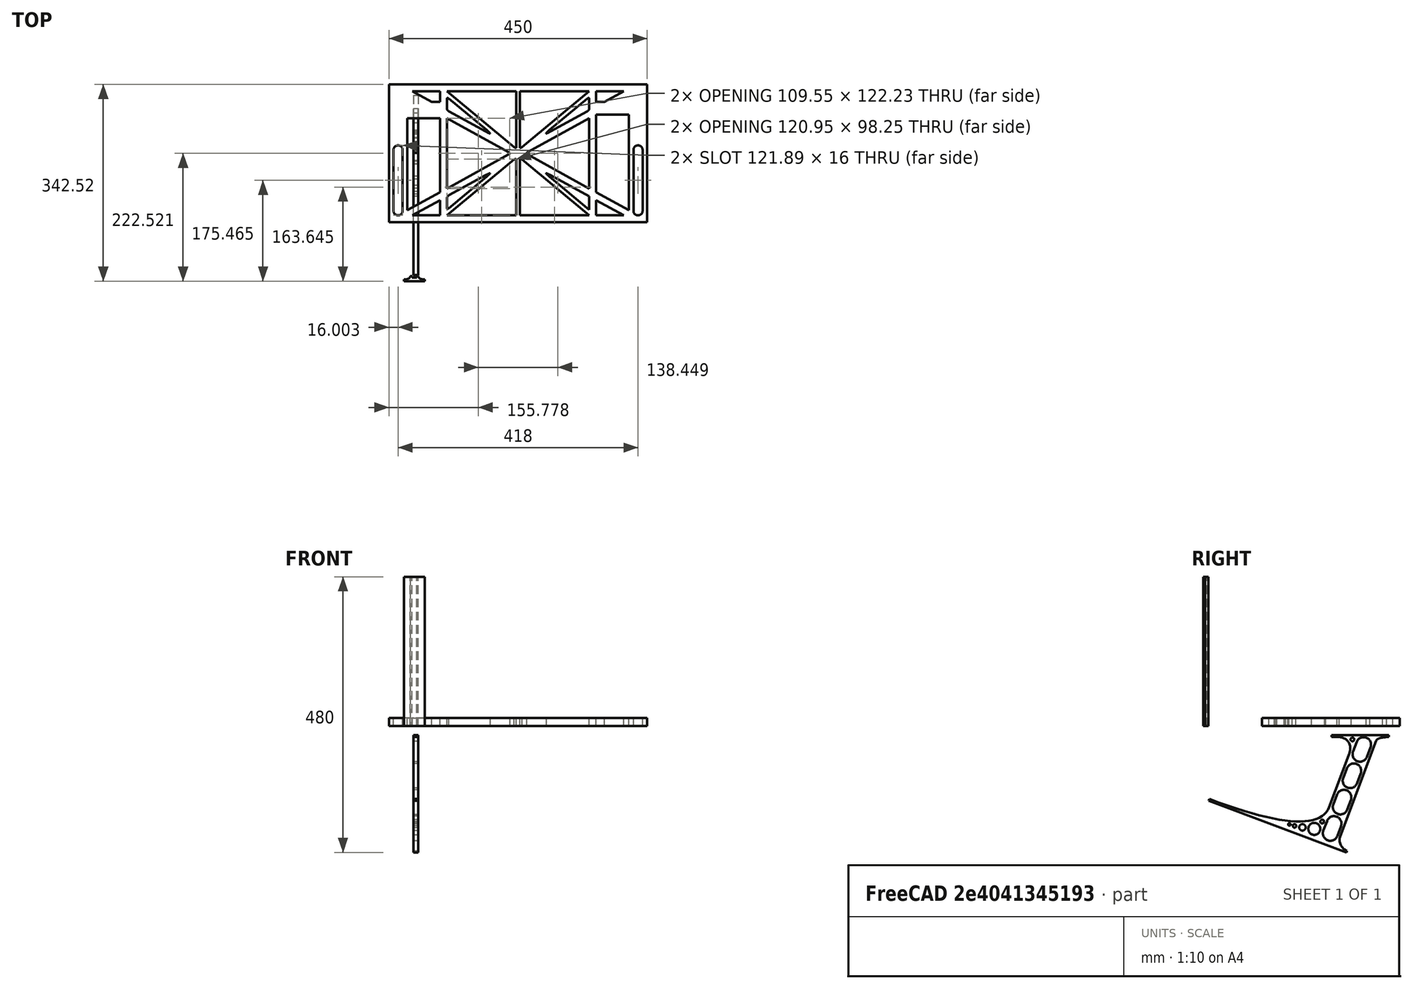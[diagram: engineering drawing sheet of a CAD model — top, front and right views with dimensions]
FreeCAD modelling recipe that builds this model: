
FCSTD DOCUMENT  (FreeCAD 0.19R0.19.2)
Label: laptopStand074
License: All rights reserved
LicenseURL: http://en.wikipedia.org/wiki/All_rights_reserved
objects: Sketcher::SketchObject×3, Part::Extrusion×3
note: 6 computed .brp shape members not serialized (recipe doc carries the construction recipe); baked Part::Feature solids carry a one-line shape summary decoded from their .brp

FEATURE [Sketcher::SketchObject] Sketch
  FullyConstrained = true
  sketch-geometry (164):
    g0: LineSegment StartX=-10.9272 StartY=-82.7794 StartZ=0 EndX=46.0728 EndY=-51.4823 EndZ=0
    g1: LineSegment StartX=366.073 StartY=-91.7794 StartZ=0 EndX=318.073 EndY=-65.424 EndZ=0
    g2: LineSegment StartX=-10.9272 StartY=77.3346 StartZ=0 EndX=-10.9272 EndY=-82.7794 EndZ=0
    g3: LineSegment StartX=375.073 StartY=-82.7794 StartZ=0 EndX=375.073 EndY=83.9235 EndZ=0
    g4: LineSegment StartX=-1.92719 StartY=-91.7794 StartZ=0 EndX=46.0728 EndY=-91.7794 EndZ=0
    g5: LineSegment StartX=318.073 StartY=124.221 StartZ=0 EndX=366.073 EndY=124.221 EndZ=0
    g6: LineSegment StartX=306.073 StartY=124.221 StartZ=0 EndX=189.124 EndY=27.0628 EndZ=0
    g7: LineSegment StartX=58.0728 StartY=-91.7794 StartZ=0 EndX=175.022 EndY=5.37834 EndZ=0
    g8: LineSegment StartX=58.0728 StartY=-81.8102 StartZ=0 EndX=58.0728 EndY=-58.8351 EndZ=0
    g9: LineSegment StartX=175.022 StartY=27.0628 StartZ=0 EndX=58.0728 EndY=124.221 EndZ=0
    g10: LineSegment StartX=189.124 StartY=5.37834 StartZ=0 EndX=306.073 EndY=-91.7794 EndZ=0
    g11: LineSegment StartX=306.073 StartY=77.3346 StartZ=0 EndX=306.073 EndY=-44.8935 EndZ=0
    g12: LineSegment StartX=318.073 StartY=83.9235 StartZ=0 EndX=318.073 EndY=-51.4823 EndZ=0
    g13: LineSegment StartX=306.073 StartY=-58.8351 StartZ=0 EndX=306.073 EndY=-81.8102 EndZ=0
    g14: LineSegment StartX=318.073 StartY=-51.4823 StartZ=0 EndX=375.073 EndY=-82.7794 EndZ=0
    g15: LineSegment StartX=318.073 StartY=-65.424 StartZ=0 EndX=318.073 EndY=-91.7794 EndZ=0
    g16: LineSegment StartX=318.073 StartY=-91.7794 StartZ=0 EndX=366.073 EndY=-91.7794 EndZ=0
    g17: LineSegment StartX=58.0728 StartY=-44.8935 StartZ=0 EndX=58.0728 EndY=77.3346 EndZ=0
    g18: LineSegment StartX=46.0728 StartY=-65.424 StartZ=0 EndX=-1.92719 EndY=-91.7794 EndZ=0
    g19: LineSegment StartX=46.0728 StartY=-65.424 StartZ=0 EndX=46.0728 EndY=-91.7794 EndZ=0
    g20: LineSegment StartX=46.0728 StartY=77.3346 StartZ=0 EndX=46.0728 EndY=-51.4823 EndZ=0
    g21: LineSegment StartX=-42.9272 StartY=136.221 StartZ=0 EndX=-42.9272 EndY=-103.779 EndZ=0
    g22: LineSegment StartX=407.073 StartY=136.221 StartZ=0 EndX=407.073 EndY=-103.779 EndZ=0
    g23: LineSegment StartX=179.022 StartY=27.0628 StartZ=0 EndX=179.022 EndY=124.221 EndZ=0
    g24: LineSegment StartX=185.124 StartY=27.0628 StartZ=0 EndX=185.124 EndY=124.221 EndZ=0
    g25: ArcOfCircle CenterX=-26.9272 CenterY=22.1087 CenterZ=0 NormalX=0 NormalY=0 NormalZ=1 AngleXU=0 Radius=8 StartAngle=1e-16 EndAngle=3.14159
    g26: ArcOfCircle CenterX=-26.9272 CenterY=-83.7794 CenterZ=0 NormalX=0 NormalY=0 NormalZ=1 AngleXU=0 Radius=8 StartAngle=3.14159 EndAngle=6.28319
    g27: LineSegment StartX=-34.9272 StartY=22.1087 StartZ=0 EndX=-34.9272 EndY=-83.7794 EndZ=0
    g28: LineSegment StartX=-18.9272 StartY=22.1087 StartZ=0 EndX=-18.9272 EndY=-83.7794 EndZ=0
    g29: LineSegment StartX=185.124 StartY=-91.7794 StartZ=0 EndX=306.073 EndY=-91.7794 EndZ=0
    g30: LineSegment StartX=179.022 StartY=-91.7794 StartZ=0 EndX=58.0728 EndY=-91.7794 EndZ=0
    g31: LineSegment StartX=306.073 StartY=124.221 StartZ=0 EndX=185.124 EndY=124.221 EndZ=0
    g32: LineSegment StartX=179.022 StartY=124.221 StartZ=0 EndX=58.0728 EndY=124.221 EndZ=0
    g33: ArcOfCircle CenterX=391.073 CenterY=22.1087 CenterZ=0 NormalX=0 NormalY=0 NormalZ=1 AngleXU=0 Radius=8 StartAngle=-4.4e-15 EndAngle=3.14159
    g34: LineSegment StartX=399.073 StartY=22.1087 StartZ=0 EndX=399.073 EndY=-83.7794 EndZ=0
    g35: LineSegment StartX=383.073 StartY=22.1087 StartZ=0 EndX=383.073 EndY=-83.7794 EndZ=0
    g36: ArcOfCircle CenterX=391.073 CenterY=-83.7794 CenterZ=0 NormalX=0 NormalY=0 NormalZ=1 AngleXU=0 Radius=8 StartAngle=3.14159 EndAngle=6.28319
    g37: Circle CenterX=175.022 CenterY=27.0628 CenterZ=0 NormalX=0 NormalY=0 NormalZ=1 AngleXU=0 Radius=1
    g38: Circle CenterX=179.022 CenterY=24.8665 CenterZ=0 NormalX=0 NormalY=0 NormalZ=1 AngleXU=0 Radius=1
    g39: Circle CenterX=179.022 CenterY=27.0628 CenterZ=0 NormalX=0 NormalY=0 NormalZ=1 AngleXU=0 Radius=1
    g40: BSplineCurve PolesCount=3 KnotsCount=2 Degree=2 IsPeriodic=0
    g41: GeomPoint X=175.022 Y=27.0628 Z=0
    g42: GeomPoint X=179.022 Y=27.0628 Z=0
    g43: Circle CenterX=189.124 CenterY=27.0628 CenterZ=0 NormalX=0 NormalY=0 NormalZ=1 AngleXU=0 Radius=1
    g44: Circle CenterX=185.124 CenterY=24.8665 CenterZ=0 NormalX=0 NormalY=0 NormalZ=1 AngleXU=0 Radius=1
    g45: Circle CenterX=185.124 CenterY=27.0628 CenterZ=0 NormalX=0 NormalY=0 NormalZ=1 AngleXU=0 Radius=1
    g46: BSplineCurve PolesCount=3 KnotsCount=2 Degree=2 IsPeriodic=0
    g47: GeomPoint X=189.124 Y=27.0628 Z=0
    g48: GeomPoint X=185.124 Y=27.0628 Z=0
    g49: Circle CenterX=175.022 CenterY=5.37834 CenterZ=0 NormalX=0 NormalY=0 NormalZ=1 AngleXU=0 Radius=1
    g50: Circle CenterX=179.022 CenterY=7.57463 CenterZ=0 NormalX=0 NormalY=0 NormalZ=1 AngleXU=0 Radius=1
    g51: Circle CenterX=179.022 CenterY=5.34704 CenterZ=0 NormalX=0 NormalY=0 NormalZ=1 AngleXU=0 Radius=1
    g52: BSplineCurve PolesCount=3 KnotsCount=2 Degree=2 IsPeriodic=0
    g53: GeomPoint X=175.022 Y=5.37834 Z=0
    g54: GeomPoint X=179.022 Y=5.34704 Z=0
    g55: Circle CenterX=189.124 CenterY=5.37834 CenterZ=0 NormalX=0 NormalY=0 NormalZ=1 AngleXU=0 Radius=1
    g56: Circle CenterX=185.124 CenterY=7.57463 CenterZ=0 NormalX=0 NormalY=0 NormalZ=1 AngleXU=0 Radius=1
    g57: Circle CenterX=185.124 CenterY=5.34704 CenterZ=0 NormalX=0 NormalY=0 NormalZ=1 AngleXU=0 Radius=1
    g58: BSplineCurve PolesCount=3 KnotsCount=2 Degree=2 IsPeriodic=0
    g59: GeomPoint X=189.124 Y=5.37834 Z=0
    g60: GeomPoint X=185.124 Y=5.34704 Z=0
    g61: LineSegment StartX=179.022 StartY=5.34704 StartZ=0 EndX=179.022 EndY=-91.7794 EndZ=0
    g62: LineSegment StartX=185.124 StartY=-91.7794 StartZ=0 EndX=185.124 EndY=5.34704 EndZ=0
    g63: Circle CenterX=165.871 CenterY=18.1458 CenterZ=0 NormalX=0 NormalY=0 NormalZ=1 AngleXU=0 Radius=1
    g64: Circle CenterX=169.377 CenterY=16.2206 CenterZ=0 NormalX=0 NormalY=0 NormalZ=1 AngleXU=0 Radius=1
    g65: Circle CenterX=165.871 CenterY=14.2954 CenterZ=0 NormalX=0 NormalY=0 NormalZ=1 AngleXU=0 Radius=1
    g66: BSplineCurve PolesCount=3 KnotsCount=2 Degree=2 IsPeriodic=0
    g67: GeomPoint X=165.871 Y=18.1458 Z=0
    g68: GeomPoint X=165.871 Y=14.2954 Z=0
    g69: Circle CenterX=198.275 CenterY=18.1458 CenterZ=0 NormalX=0 NormalY=0 NormalZ=1 AngleXU=0 Radius=1
    g70: Circle CenterX=194.768 CenterY=16.2206 CenterZ=0 NormalX=0 NormalY=0 NormalZ=1 AngleXU=0 Radius=1
    g71: Circle CenterX=198.275 CenterY=14.2954 CenterZ=0 NormalX=0 NormalY=0 NormalZ=1 AngleXU=0 Radius=1
    g72: BSplineCurve PolesCount=3 KnotsCount=2 Degree=2 IsPeriodic=0
    g73: GeomPoint X=198.275 Y=18.1458 Z=0
    g74: GeomPoint X=198.275 Y=14.2954 Z=0
    g75: LineSegment StartX=165.871 StartY=18.1458 StartZ=0 EndX=58.0728 EndY=77.3346 EndZ=0
    g76: LineSegment StartX=58.0728 StartY=-44.8935 StartZ=0 EndX=165.871 EndY=14.2954 EndZ=0
    g77: LineSegment StartX=198.275 StartY=18.1458 StartZ=0 EndX=306.073 EndY=77.3346 EndZ=0
    g78: LineSegment StartX=198.275 StartY=14.2954 StartZ=0 EndX=306.073 EndY=-44.8935 EndZ=0
    g79: LineSegment StartX=407.073 StartY=-103.779 StartZ=0 EndX=-42.9272 EndY=-103.779 EndZ=0
    g80: LineSegment StartX=407.073 StartY=136.221 StartZ=0 EndX=-42.9272 EndY=136.221 EndZ=0
    g81: LineSegment StartX=46.0728 StartY=77.3346 StartZ=0 EndX=-10.9272 EndY=77.3346 EndZ=0
    g82: LineSegment StartX=46.0728 StartY=105.865 StartZ=0 EndX=31.5028 EndY=105.865 EndZ=0
    g83: LineSegment StartX=46.0728 StartY=124.221 StartZ=0 EndX=46.0728 EndY=105.865 EndZ=0
    g84: LineSegment StartX=-1.92719 StartY=124.221 StartZ=0 EndX=31.5028 EndY=105.865 EndZ=0
    g85: LineSegment StartX=46.0728 StartY=124.221 StartZ=0 EndX=-1.92719 EndY=124.221 EndZ=0
    g86: LineSegment StartX=318.073 StartY=83.9235 StartZ=0 EndX=375.073 EndY=83.9235 EndZ=0
    g87: LineSegment StartX=318.073 StartY=105.865 StartZ=0 EndX=332.643 EndY=105.865 EndZ=0
    g88: LineSegment StartX=332.643 StartY=105.865 StartZ=0 EndX=366.073 EndY=124.221 EndZ=0
    g89: LineSegment StartX=318.073 StartY=124.221 StartZ=0 EndX=318.073 EndY=105.865 EndZ=0
    g90: Circle CenterX=125.607 CenterY=54.1951 CenterZ=0 NormalX=0 NormalY=0 NormalZ=1 AngleXU=0 Radius=1
    g91: Circle CenterX=139.632 CenterY=46.4944 CenterZ=0 NormalX=0 NormalY=0 NormalZ=1 AngleXU=0 Radius=1
    g92: Circle CenterX=127.326 CenterY=56.7187 CenterZ=0 NormalX=0 NormalY=0 NormalZ=1 AngleXU=0 Radius=1
    g93: BSplineCurve PolesCount=3 KnotsCount=2 Degree=2 IsPeriodic=0
    g94: GeomPoint X=125.607 Y=54.1951 Z=0
    g95: GeomPoint X=127.326 Y=56.7187 Z=0
    g96: Circle CenterX=236.821 CenterY=56.7187 CenterZ=0 NormalX=0 NormalY=0 NormalZ=1 AngleXU=0 Radius=1
    g97: Circle CenterX=224.513 CenterY=46.4944 CenterZ=0 NormalX=0 NormalY=0 NormalZ=1 AngleXU=0 Radius=1
    g98: Circle CenterX=238.538 CenterY=54.1951 CenterZ=0 NormalX=0 NormalY=0 NormalZ=1 AngleXU=0 Radius=1
    g99: BSplineCurve PolesCount=3 KnotsCount=2 Degree=2 IsPeriodic=0
    g100: GeomPoint X=236.821 Y=56.7187 Z=0
    g101: GeomPoint X=238.538 Y=54.1951 Z=0
    g102: Circle CenterX=238.538 CenterY=-21.7539 CenterZ=0 NormalX=0 NormalY=0 NormalZ=1 AngleXU=0 Radius=1
    g103: Circle CenterX=224.513 CenterY=-14.0532 CenterZ=0 NormalX=0 NormalY=0 NormalZ=1 AngleXU=0 Radius=1
    g104: Circle CenterX=236.821 CenterY=-24.2775 CenterZ=0 NormalX=0 NormalY=0 NormalZ=1 AngleXU=0 Radius=1
    g105: BSplineCurve PolesCount=3 KnotsCount=2 Degree=2 IsPeriodic=0
    g106: GeomPoint X=238.538 Y=-21.7539 Z=0
    g107: GeomPoint X=236.821 Y=-24.2775 Z=0
    g108: LineSegment StartX=238.538 StartY=-21.7539 StartZ=0 EndX=306.073 EndY=-58.8351 EndZ=0
    g109: LineSegment StartX=236.821 StartY=-24.2775 StartZ=0 EndX=306.073 EndY=-81.8102 EndZ=0
    g110: Circle CenterX=125.607 CenterY=-21.7539 CenterZ=0 NormalX=0 NormalY=0 NormalZ=1 AngleXU=0 Radius=1
    g111: Circle CenterX=139.632 CenterY=-14.0532 CenterZ=0 NormalX=0 NormalY=0 NormalZ=1 AngleXU=0 Radius=1
    g112: Circle CenterX=127.325 CenterY=-24.2775 CenterZ=0 NormalX=0 NormalY=0 NormalZ=1 AngleXU=0 Radius=1
    g113: BSplineCurve PolesCount=3 KnotsCount=2 Degree=2 IsPeriodic=0
    g114: GeomPoint X=125.607 Y=-21.7539 Z=0
    g115: GeomPoint X=127.325 Y=-24.2775 Z=0
    g116: LineSegment StartX=125.607 StartY=-21.7539 StartZ=0 EndX=58.0728 EndY=-58.8351 EndZ=0
    g117: LineSegment StartX=127.325 StartY=-24.2775 StartZ=0 EndX=58.0728 EndY=-81.8102 EndZ=0
    g118: Circle CenterX=302.996 CenterY=111.695 CenterZ=0 NormalX=0 NormalY=0 NormalZ=1 AngleXU=0 Radius=1
    g119: Circle CenterX=306.073 CenterY=114.251 CenterZ=0 NormalX=0 NormalY=0 NormalZ=1 AngleXU=0 Radius=1
    g120: Circle CenterX=306.073 CenterY=110.251 CenterZ=0 NormalX=0 NormalY=0 NormalZ=1 AngleXU=0 Radius=1
    g121: BSplineCurve PolesCount=3 KnotsCount=2 Degree=2 IsPeriodic=0
    g122: GeomPoint X=302.996 Y=111.695 Z=0
    g123: GeomPoint X=306.073 Y=110.251 Z=0
    g124: Circle CenterX=306.073 CenterY=95.2763 CenterZ=0 NormalX=0 NormalY=0 NormalZ=1 AngleXU=0 Radius=1
    g125: Circle CenterX=306.073 CenterY=91.2763 CenterZ=0 NormalX=0 NormalY=0 NormalZ=1 AngleXU=0 Radius=1
    g126: Circle CenterX=302.567 CenterY=89.3511 CenterZ=0 NormalX=0 NormalY=0 NormalZ=1 AngleXU=0 Radius=1
    g127: BSplineCurve PolesCount=3 KnotsCount=2 Degree=2 IsPeriodic=0
    g128: GeomPoint X=306.073 Y=95.2763 Z=0
    g129: GeomPoint X=302.567 Y=89.3511 Z=0
    g130: LineSegment StartX=306.073 StartY=110.251 StartZ=0 EndX=306.073 EndY=95.2763 EndZ=0
    g131: LineSegment StartX=302.996 StartY=111.695 StartZ=0 EndX=236.821 EndY=56.7187 EndZ=0
    g132: LineSegment StartX=238.538 StartY=54.1951 StartZ=0 EndX=302.567 EndY=89.3511 EndZ=0
    g133: Circle CenterX=61.1496 CenterY=111.695 CenterZ=0 NormalX=0 NormalY=0 NormalZ=1 AngleXU=0 Radius=1
    g134: Circle CenterX=58.0728 CenterY=114.251 CenterZ=0 NormalX=0 NormalY=0 NormalZ=1 AngleXU=0 Radius=1
    g135: Circle CenterX=58.0728 CenterY=110.251 CenterZ=0 NormalX=0 NormalY=0 NormalZ=1 AngleXU=0 Radius=1
    g136: BSplineCurve PolesCount=3 KnotsCount=2 Degree=2 IsPeriodic=0
    g137: GeomPoint X=61.1496 Y=111.695 Z=0
    g138: GeomPoint X=58.0728 Y=110.251 Z=0
    g139: Circle CenterX=61.5791 CenterY=89.3511 CenterZ=0 NormalX=0 NormalY=0 NormalZ=1 AngleXU=0 Radius=1
    g140: Circle CenterX=58.0728 CenterY=91.2763 CenterZ=0 NormalX=0 NormalY=0 NormalZ=1 AngleXU=0 Radius=1
    g141: Circle CenterX=58.0728 CenterY=95.2763 CenterZ=0 NormalX=0 NormalY=0 NormalZ=1 AngleXU=0 Radius=1
    g142: BSplineCurve PolesCount=3 KnotsCount=2 Degree=2 IsPeriodic=0
    g143: GeomPoint X=61.5791 Y=89.3511 Z=0
    g144: GeomPoint X=58.0728 Y=95.2763 Z=0
    g145: LineSegment StartX=58.0728 StartY=110.251 StartZ=0 EndX=58.0728 EndY=95.2763 EndZ=0
    g146: LineSegment StartX=61.1496 StartY=111.695 StartZ=0 EndX=127.326 EndY=56.7187 EndZ=0
    g147: LineSegment StartX=125.607 StartY=54.1951 StartZ=0 EndX=61.5791 EndY=89.3511 EndZ=0
    g148: LineSegment StartX=58.0728 StartY=-58.8351 StartZ=0 EndX=58.0728 EndY=-62.8351 EndZ=0
    g149: LineSegment StartX=58.0728 StartY=-58.8351 StartZ=0 EndX=61.5791 EndY=-56.9099 EndZ=0
    g150: LineSegment StartX=58.0728 StartY=-81.8102 StartZ=0 EndX=61.1496 EndY=-79.2541 EndZ=0
    g151: LineSegment StartX=58.0728 StartY=-81.8102 StartZ=0 EndX=58.0728 EndY=-77.8102 EndZ=0
    g152: Circle CenterX=61.5791 CenterY=-56.9099 CenterZ=0 NormalX=0 NormalY=0 NormalZ=1 AngleXU=0 Radius=1
    g153: Circle CenterX=58.0728 CenterY=-58.8351 CenterZ=0 NormalX=0 NormalY=0 NormalZ=1 AngleXU=0 Radius=1
    g154: Circle CenterX=58.0728 CenterY=-62.8351 CenterZ=0 NormalX=0 NormalY=0 NormalZ=1 AngleXU=0 Radius=1
    g155: BSplineCurve PolesCount=3 KnotsCount=2 Degree=2 IsPeriodic=0
    g156: GeomPoint X=61.5791 Y=-56.9099 Z=0
    g157: GeomPoint X=58.0728 Y=-62.8351 Z=0
    g158: Circle CenterX=58.0728 CenterY=-77.8102 CenterZ=0 NormalX=0 NormalY=0 NormalZ=1 AngleXU=0 Radius=1
    g159: Circle CenterX=58.0728 CenterY=-81.8102 CenterZ=0 NormalX=0 NormalY=0 NormalZ=1 AngleXU=0 Radius=1
    g160: Circle CenterX=61.1496 CenterY=-79.2541 CenterZ=0 NormalX=0 NormalY=0 NormalZ=1 AngleXU=0 Radius=1
    g161: BSplineCurve PolesCount=3 KnotsCount=2 Degree=2 IsPeriodic=0
    g162: GeomPoint X=58.0728 Y=-77.8102 Z=0
    g163: GeomPoint X=61.1496 Y=-79.2541 Z=0
  constraints (295):
    c: Horizontal(g4)
    c: Horizontal(g5)
    c: Tangent(g11,g13)
    c: Coincident(g12,g14)
    c: Coincident(g15,g1)
    c: Tangent(g12,g15)
    c: Coincident(g19,g18)
    c: Coincident(g0,g20)
    c: Block(g9)
    c: Block(g6)
    c: Block(g14)
    c: Block(g3)
    c: Block(g13)
    c: Block(g1)
    c: Block(g15)
    c: Block(g10)
    c: Block(g7)
    c: Block(g19)
    c: Block(g18)
    c: Block(g0)
    c: Block(g2)
    c: Block(g11)
    c: Block(g5)
    c: Block(g16)
    c: Block(g4)
    c: Vertical(g21)
    c: Vertical(g22)
    c: Block(g22)
    c: Block(g21)
    c: Vertical(g23)
    c: Vertical(g24)
    c: Block(g23)
    c: Block(g24)
    c: Tangent(g25,g28) = 1.5708
    c: Tangent(g25,g27) = -1.5708
    c: Tangent(g27,g26) = -1.5708
    c: Tangent(g28,g26) = 1.5708
    c: Vertical(g27)
    c: Equal(g25,g26)
    c: Block(g28)
    c: Block(g27)
    c: Coincident(g29,g10)
    c: Horizontal(g29)
    c: Coincident(g30,g7)
    c: Horizontal(g30)
    c: Coincident(g31,g6)
    c: Coincident(g31,g24)
    c: Horizontal(g31)
    c: Coincident(g32,g23)
    c: Coincident(g32,g9)
    c: Horizontal(g32)
    c: Tangent(g33,g34) = 1.5708
    c: Tangent(g34,g36) = 1.5708
    c: Equal(g33,g36)
    c: Coincident(g35,g33)
    c: Coincident(g35,g36)
    c: Block(g34)
    c: Block(g35)
    c: Coincident(g40,g9)
    c: Weight(g37) = 1
    c: Equal(g37,g38)
    c: Equal(g37,g39)
    c: Coincident(g40,g23)
    c: InternalAlignment(g37,g40)
    c: InternalAlignment(g38,g40)
    c: InternalAlignment(g39,g40)
    c: InternalAlignment(g41,g40)
    c: InternalAlignment(g42,g40)
    c: Coincident(g46,g6)
    c: Weight(g43) = 1
    c: Equal(g43,g44)
    c: Equal(g43,g45)
    c: Coincident(g46,g24)
    c: InternalAlignment(g43,g46)
    c: InternalAlignment(g44,g46)
    c: InternalAlignment(g45,g46)
    c: InternalAlignment(g47,g46)
    c: InternalAlignment(g48,g46)
    c: Block(g46)
    c: Block(g40)
    c: Coincident(g52,g7)
    c: Weight(g49) = 1
    c: Equal(g49,g50)
    c: Equal(g49,g51)
    c: InternalAlignment(g49,g52)
    c: InternalAlignment(g50,g52)
    c: InternalAlignment(g51,g52)
    c: InternalAlignment(g53,g52)
    c: InternalAlignment(g54,g52)
    c: Weight(g55) = 1
    c: Equal(g55,g56)
    c: Equal(g55,g57)
    c: InternalAlignment(g55,g58)
    c: InternalAlignment(g56,g58)
    c: InternalAlignment(g57,g58)
    c: InternalAlignment(g59,g58)
    c: InternalAlignment(g60,g58)
    c: Block(g58)
    c: Block(g52)
    c: Coincident(g61,g52)
    c: Coincident(g61,g30)
    c: Vertical(g61)
    c: Coincident(g62,g29)
    c: Coincident(g62,g58)
    c: Vertical(g62)
    c: Weight(g63) = 1
    c: Equal(g63,g64)
    c: Equal(g63,g65)
    c: InternalAlignment(g63,g66)
    c: InternalAlignment(g64,g66)
    c: InternalAlignment(g65,g66)
    c: InternalAlignment(g67,g66)
    c: InternalAlignment(g68,g66)
    c: Weight(g69) = 1
    c: Equal(g69,g70)
    c: Equal(g69,g71)
    c: InternalAlignment(g69,g72)
    c: InternalAlignment(g70,g72)
    c: InternalAlignment(g71,g72)
    c: InternalAlignment(g73,g72)
    c: InternalAlignment(g74,g72)
    c: Block(g66)
    c: Block(g72)
    c: Coincident(g75,g66)
    c: Coincident(g75,g17)
    c: Coincident(g76,g17)
    c: Coincident(g76,g66)
    c: Coincident(g77,g72)
    c: Coincident(g77,g11)
    c: Coincident(g78,g72)
    c: Coincident(g78,g11)
    c: Block(g17)
    c: Coincident(g79,g22)
    c: Coincident(g79,g21)
    c: Horizontal(g79)
    c: Distance(g79) = 450
    c: Coincident(g80,g22)
    c: Coincident(g80,g21)
    c: Horizontal(g80)
    c: Horizontal(g81)
    c: Coincident(g20,g81)
    c: Horizontal(g82)
    c: Vertical(g83)
    c: Block(g83)
    c: Block(g82)
    c: Block(g81)
    c: Distance(g83) = 18.3554
    c: Coincident(g85,g83)
    c: Coincident(g85,g84)
    c: Horizontal(g85)
    c: Block(g85)
    c: Block(g84)
    c: Coincident(g82,g84)
    c: Coincident(g2,g81)
    c: Coincident(g86,g12)
    c: Horizontal(g86)
    c: Horizontal(g87)
    c: Block(g86)
    c: Coincident(g88,g5)
    c: Coincident(g89,g5)
    c: Coincident(g89,g87)
    c: Vertical(g89)
    c: Block(g89)
    c: Coincident(g87,g88)
    c: Block(g88)
    c: Coincident(g3,g86)
    c: Weight(g90) = 1
    c: Equal(g90,g91)
    c: Equal(g90,g92)
    c: InternalAlignment(g90,g93)
    c: InternalAlignment(g91,g93)
    c: InternalAlignment(g92,g93)
    c: InternalAlignment(g94,g93)
    c: InternalAlignment(g95,g93)
    c: Block(g93)
    c: Weight(g96) = 1
    c: Equal(g96,g97)
    c: Equal(g96,g98)
    c: InternalAlignment(g96,g99)
    c: InternalAlignment(g97,g99)
    c: InternalAlignment(g98,g99)
    c: InternalAlignment(g100,g99)
    c: InternalAlignment(g101,g99)
    c: Block(g99)
    c: Weight(g102) = 1
    c: Equal(g102,g103)
    c: Equal(g102,g104)
    c: InternalAlignment(g102,g105)
    c: InternalAlignment(g103,g105)
    c: InternalAlignment(g104,g105)
    c: InternalAlignment(g106,g105)
    c: InternalAlignment(g107,g105)
    c: Block(g105)
    c: Coincident(g108,g105)
    c: Coincident(g108,g13)
    c: Coincident(g109,g105)
    c: Coincident(g109,g13)
    c: Weight(g110) = 1
    c: Equal(g110,g111)
    c: Equal(g110,g112)
    c: InternalAlignment(g110,g113)
    c: InternalAlignment(g111,g113)
    c: InternalAlignment(g112,g113)
    c: InternalAlignment(g114,g113)
    c: InternalAlignment(g115,g113)
    c: Block(g113)
    c: Coincident(g116,g113)
    c: Coincident(g116,g8)
    c: Coincident(g117,g113)
    c: Coincident(g117,g8)
    c: Block(g8)
    c: Weight(g118) = 1
    c: Equal(g118,g119)
    c: Equal(g118,g120)
    c: InternalAlignment(g118,g121)
    c: InternalAlignment(g119,g121)
    c: InternalAlignment(g120,g121)
    c: InternalAlignment(g122,g121)
    c: InternalAlignment(g123,g121)
    c: Weight(g124) = 1
    c: Equal(g124,g125)
    c: Equal(g124,g126)
    c: InternalAlignment(g124,g127)
    c: InternalAlignment(g125,g127)
    c: InternalAlignment(g126,g127)
    c: InternalAlignment(g128,g127)
    c: InternalAlignment(g129,g127)
    c: Block(g121)
    c: Block(g127)
    c: Coincident(g130,g121)
    c: Coincident(g130,g127)
    c: Vertical(g130)
    c: Coincident(g131,g121)
    c: Coincident(g131,g99)
    c: Coincident(g132,g99)
    c: Coincident(g132,g127)
    c: Weight(g133) = 1
    c: Equal(g133,g134)
    c: Equal(g133,g135)
    c: InternalAlignment(g133,g136)
    c: InternalAlignment(g134,g136)
    c: InternalAlignment(g135,g136)
    c: InternalAlignment(g137,g136)
    c: InternalAlignment(g138,g136)
    c: Weight(g139) = 1
    c: Equal(g139,g140)
    c: Equal(g139,g141)
    c: InternalAlignment(g139,g142)
    c: InternalAlignment(g140,g142)
    c: InternalAlignment(g141,g142)
    c: InternalAlignment(g143,g142)
    c: InternalAlignment(g144,g142)
    c: Block(g136)
    c: Block(g142)
    c: Coincident(g145,g136)
    c: Coincident(g145,g142)
    c: Vertical(g145)
    c: Coincident(g146,g136)
    c: Coincident(g146,g93)
    c: Coincident(g147,g93)
    c: Coincident(g147,g142)
    c: Vertical(g148)
    c: Vertical(g151)
    c: Parallel(g117,g150)
    c: Parallel(g116,g149)
    c: Distance(g149) = 4
    c: Distance(g148) = 4
    c: Distance(g151) = 4
    c: Distance(g150) = 4
    c: Coincident(g149,g8)
    c: Coincident(g148,g8)
    c: Coincident(g8,g151)
    c: Coincident(g150,g8)
    c: Coincident(g155,g149)
    c: Weight(g152) = 1
    c: Equal(g152,g153)
    c: Coincident(g153,g8)
    c: Equal(g152,g154)
    c: Coincident(g155,g148)
    c: InternalAlignment(g152,g155)
    c: InternalAlignment(g153,g155)
    c: InternalAlignment(g154,g155)
    c: InternalAlignment(g156,g155)
    c: InternalAlignment(g157,g155)
    c: Coincident(g161,g151)
    c: Weight(g158) = 1
    c: Equal(g158,g159)
    c: Coincident(g159,g8)
    c: Equal(g158,g160)
    c: Coincident(g161,g150)
    c: InternalAlignment(g158,g161)
    c: InternalAlignment(g159,g161)
    c: InternalAlignment(g160,g161)
    c: InternalAlignment(g162,g161)
    c: InternalAlignment(g163,g161)
FEATURE [Sketcher::SketchObject] Sketch001
  FullyConstrained = true
  MapMode = 4
  Placement = pos=(0,0,0) rot=(0.57735,0.57735,0.57735;2.0944rad)
  Support = -> [Sketch]
  sketch-geometry (46):
    g0: BSplineCurve PolesCount=3 KnotsCount=2 Degree=2 IsPeriodic=0
    g1: ArcOfCircle CenterX=73.1223 CenterY=-32.291 CenterZ=0 NormalX=0 NormalY=0 NormalZ=1 AngleXU=0 Radius=13 StartAngle=5.92268 EndAngle=9.06428
    g2: ArcOfCircle CenterX=66.7816 CenterY=-49.1439 CenterZ=0 NormalX=0 NormalY=0 NormalZ=1 AngleXU=0 Radius=13 StartAngle=2.78068 EndAngle=5.92131
    g3: ArcOfCircle CenterX=55.9263 CenterY=-78.1807 CenterZ=0 NormalX=0 NormalY=0 NormalZ=1 AngleXU=0 Radius=13 StartAngle=5.92268 EndAngle=9.06428
    g4: ArcOfCircle CenterX=49.5884 CenterY=-95.0342 CenterZ=0 NormalX=0 NormalY=0 NormalZ=1 AngleXU=0 Radius=13 StartAngle=2.78068 EndAngle=5.92131
    g5: ArcOfCircle CenterX=38.7206 CenterY=-124.067 CenterZ=0 NormalX=0 NormalY=0 NormalZ=1 AngleXU=0 Radius=13 StartAngle=5.92268 EndAngle=9.06428
    g6: ArcOfCircle CenterX=32.3875 CenterY=-140.92 CenterZ=0 NormalX=0 NormalY=0 NormalZ=1 AngleXU=0 Radius=13 StartAngle=2.78068 EndAngle=5.92131
    g7: ArcOfCircle CenterX=21.4715 CenterY=-169.934 CenterZ=0 NormalX=0 NormalY=0 NormalZ=1 AngleXU=0 Radius=13 StartAngle=5.92268 EndAngle=9.06428
    g8: ArcOfCircle CenterX=15.1336 CenterY=-186.787 CenterZ=0 NormalX=0 NormalY=0 NormalZ=1 AngleXU=0 Radius=13 StartAngle=2.78068 EndAngle=5.92131
    g9-g12: Circle x4 (B-spline internal-alignment scaffolding for g13; pole/knot coordinates omitted)
    g13: BSplineCurve PolesCount=4 KnotsCount=2 Degree=3 IsPeriodic=0
    g14: GeomPoint X=28.8094 Y=-19.0875 Z=0
    g15: GeomPoint X=47.0443 Y=-50.4712 Z=0
    g16: Circle CenterX=53.5586 CenterY=-23.2695 CenterZ=0 NormalX=0 NormalY=0 NormalZ=1 AngleXU=0 Radius=3.24518
    g17: Circle CenterX=-195.441 CenterY=-127.082 CenterZ=0 NormalX=0 NormalY=0 NormalZ=1 AngleXU=0 Radius=1
    g18: Circle CenterX=-8.24091 CenterY=-197.481 CenterZ=0 NormalX=0 NormalY=0 NormalZ=1 AngleXU=0 Radius=1
    g19: Circle CenterX=12.8789 CenterY=-141.321 CenterZ=0 NormalX=0 NormalY=0 NormalZ=1 AngleXU=0 Radius=1
    g20: BSplineCurve PolesCount=3 KnotsCount=2 Degree=2 IsPeriodic=0
    g21: GeomPoint X=-195.441 Y=-127.082 Z=0
    g22: GeomPoint X=12.8789 Y=-141.321 Z=0
    g23: Circle CenterX=-12.8016 CenterY=-179.036 CenterZ=0 NormalX=0 NormalY=0 NormalZ=1 AngleXU=0 Radius=10.5072
    g24: Circle CenterX=0.933922 CenterY=-166.43 CenterZ=0 NormalX=0 NormalY=0 NormalZ=1 AngleXU=0 Radius=3.26661
    g25: Circle CenterX=-33.5518 CenterY=-176.44 CenterZ=0 NormalX=0 NormalY=0 NormalZ=1 AngleXU=0 Radius=5.64388
    g26: Circle CenterX=-47.2366 CenterY=-173.859 CenterZ=0 NormalX=0 NormalY=0 NormalZ=1 AngleXU=0 Radius=3.01653
    g27: Circle CenterX=-56.2595 CenterY=-171.456 CenterZ=0 NormalX=0 NormalY=0 NormalZ=1 AngleXU=0 Radius=2.12826
    g28: ArcOfCircle CenterX=51.2151 CenterY=-198.473 CenterZ=0 NormalX=0 NormalY=0 NormalZ=1 AngleXU=0 Radius=20 StartAngle=2.78189 EndAngle=4.35269
    g29: LineSegment StartX=32.4951 StartY=-191.433 StartZ=0 EndX=94.6578 EndY=-26.1352 EndZ=0
    g30: LineSegment StartX=43.1192 StartY=-220.001 StartZ=0 EndX=-196.497 EndY=-129.89 EndZ=0
    g31: LineSegment StartX=43.1192 StartY=-220.001 StartZ=0 EndX=44.1752 EndY=-217.193 EndZ=0
    g32: LineSegment StartX=117.223 StartY=-19.0875 StartZ=0 EndX=117.223 EndY=-16.0875 EndZ=0
    g33: LineSegment StartX=117.223 StartY=-16.0875 StartZ=0 EndX=17.2232 EndY=-16.0875 EndZ=0
    g34: LineSegment StartX=17.2232 StartY=-16.0875 StartZ=0 EndX=17.2232 EndY=-19.0875 EndZ=0
    g35: LineSegment StartX=28.8094 StartY=-19.0875 StartZ=0 EndX=17.2232 EndY=-19.0875 EndZ=0
    g36: LineSegment StartX=47.0443 StartY=-50.4712 StartZ=0 EndX=12.8789 EndY=-141.321 EndZ=0
    g37: LineSegment StartX=-195.441 StartY=-127.082 StartZ=0 EndX=-196.497 EndY=-129.89 EndZ=0
    g38: LineSegment StartX=85.2866 StartY=-36.8766 StartZ=0 EndX=78.9396 EndY=-53.7463 EndZ=0
    g39: LineSegment StartX=60.9579 StartY=-27.7053 StartZ=0 EndX=54.6191 EndY=-44.5532 EndZ=0
    g40: LineSegment StartX=68.0907 StartY=-82.7664 StartZ=0 EndX=61.7465 EndY=-99.6365 EndZ=0
    g41: LineSegment StartX=43.7619 StartY=-73.595 StartZ=0 EndX=37.426 EndY=-90.4435 EndZ=0
    g42: LineSegment StartX=50.885 StartY=-128.652 StartZ=0 EndX=44.5456 EndY=-145.522 EndZ=0
    g43: LineSegment StartX=26.5562 StartY=-119.481 StartZ=0 EndX=20.2251 EndY=-136.329 EndZ=0
    g44: LineSegment StartX=9.3071 StartY=-165.349 StartZ=0 EndX=2.97115 EndY=-182.197 EndZ=0
    g45: LineSegment StartX=33.6358 StartY=-174.52 StartZ=0 EndX=27.2917 EndY=-191.39 EndZ=0
  constraints (71):
    c: Block(g0)
    c: Block(g1)
    c: Block(g2)
    c: Block(g4)
    c: Block(g3)
    c: Block(g6)
    c: Block(g5)
    c: Block(g8)
    c: Block(g7)
    c: Weight(g9) = 1
    c: Equal(g9,g10)
    c: Equal(g9,g11)
    c: Equal(g9,g12)
    c: InternalAlignment(g9-g12 -> g13) x4
    c: InternalAlignment(g14,g13)
    c: InternalAlignment(g15,g13)
    c: Block(g16)
    c: Weight(g17) = 1
    c: Equal(g17,g18)
    c: Equal(g17,g19)
    c: InternalAlignment(g17,g20)
    c: InternalAlignment(g18,g20)
    c: InternalAlignment(g19,g20)
    c: InternalAlignment(g21,g20)
    c: InternalAlignment(g22,g20)
    c: Block(g20)
    c: Block(g23)
    c: Block(g24)
    c: Block(g25)
    c: Block(g26)
    c: Block(g27)
    c: Block(g28)
    c: Coincident(g29,g28)
    c: Coincident(g29,g0)
    c: Block(g13)
    c: Coincident(g31,g30)
    c: Coincident(g31,g28)
    c: Block(g31)
    c: Coincident(g32,g0)
    c: Vertical(g32)
    c: Coincident(g33,g32)
    c: Horizontal(g33)
    c: Coincident(g34,g33)
    c: Vertical(g34)
    c: Block(g33)
    c: Coincident(g35,g13)
    c: Coincident(g35,g34)
    c: Horizontal(g35)
    c: Coincident(g36,g13)
    c: Coincident(g36,g20)
    c: Coincident(g37,g20)
    c: Coincident(g37,g30)
    c: Block(g30)
    c: Coincident(g38,g1)
    c: Coincident(g38,g2)
    c: Coincident(g39,g1)
    c: Coincident(g39,g2)
    c: Coincident(g40,g3)
    c: Coincident(g40,g4)
    c: Coincident(g41,g3)
    c: Coincident(g41,g4)
    c: Coincident(g42,g5)
    c: Coincident(g42,g6)
    c: Coincident(g43,g5)
    c: Coincident(g43,g6)
    c: Coincident(g44,g7)
    c: Coincident(g44,g8)
    c: Coincident(g45,g7)
    c: Coincident(g45,g8)
    c: Distance(g30) = 256
    c: Distance(g33) = 100
FEATURE [Part::Extrusion] Extrude002
  Base = -> Sketch001
  Dir = (1,0,0)
  DirMode = 2
  FaceMakerClass = Part::FaceMakerBullseye
  LengthFwd = 8
  LengthRev = 0
  Solid = true
  Symmetric = false
FEATURE [Sketcher::SketchObject] Sketch002
  FullyConstrained = true
  sketch-geometry (20):
    g0: LineSegment StartX=-2.77179 StartY=-200.304 StartZ=0 EndX=5.22821 EndY=-200.304 EndZ=0
    g1: LineSegment StartX=5.22821 StartY=-200.304 StartZ=0 EndX=5.22821 EndY=-197.304 EndZ=0
    g2: LineSegment StartX=-2.77179 StartY=-200.304 StartZ=0 EndX=-2.77179 EndY=-197.304 EndZ=0
    g3: LineSegment StartX=5.22821 StartY=-197.304 StartZ=0 EndX=8.22821 EndY=-197.304 EndZ=0
    g4: LineSegment StartX=-2.77179 StartY=-197.304 StartZ=0 EndX=-5.77179 EndY=-197.304 EndZ=0
    g5: LineSegment StartX=19.2282 StartY=-203.304 StartZ=0 EndX=19.2282 EndY=-206.304 EndZ=0
    g6: LineSegment StartX=-16.7718 StartY=-203.304 StartZ=0 EndX=-16.7718 EndY=-206.304 EndZ=0
    g7: LineSegment StartX=-16.7718 StartY=-206.304 StartZ=0 EndX=19.2282 EndY=-206.304 EndZ=0
    g8: Circle CenterX=-16.7718 CenterY=-203.304 CenterZ=0 NormalX=0 NormalY=0 NormalZ=1 AngleXU=0 Radius=1
    g9: Circle CenterX=-5.77179 CenterY=-203.304 CenterZ=0 NormalX=0 NormalY=0 NormalZ=1 AngleXU=0 Radius=1
    g10: Circle CenterX=-5.77179 CenterY=-197.304 CenterZ=0 NormalX=0 NormalY=0 NormalZ=1 AngleXU=0 Radius=1
    g11: BSplineCurve PolesCount=3 KnotsCount=2 Degree=2 IsPeriodic=0
    g12: GeomPoint X=-16.7718 Y=-203.304 Z=0
    g13: GeomPoint X=-5.77179 Y=-197.304 Z=0
    g14: Circle CenterX=19.2282 CenterY=-203.304 CenterZ=0 NormalX=0 NormalY=0 NormalZ=1 AngleXU=0 Radius=1
    g15: Circle CenterX=8.22821 CenterY=-203.304 CenterZ=0 NormalX=0 NormalY=0 NormalZ=1 AngleXU=0 Radius=1
    g16: Circle CenterX=8.22821 CenterY=-197.304 CenterZ=0 NormalX=0 NormalY=0 NormalZ=1 AngleXU=0 Radius=1
    g17: BSplineCurve PolesCount=3 KnotsCount=2 Degree=2 IsPeriodic=0
    g18: GeomPoint X=19.2282 Y=-203.304 Z=0
    g19: GeomPoint X=8.22821 Y=-197.304 Z=0
  constraints (41):
    c: Horizontal(g0)
    c: Distance(g0) = 8
    c: Coincident(g1,g0)
    c: Vertical(g1)
    c: Distance(g1) = 3
    c: Coincident(g2,g0)
    c: Vertical(g2)
    c: Distance(g2) = 3
    c: Coincident(g3,g1)
    c: Horizontal(g3)
    c: Distance(g3) = 3
    c: Coincident(g4,g2)
    c: Horizontal(g4)
    c: Distance(g4) = 3
    c: Vertical(g5)
    c: Vertical(g6)
    c: Coincident(g7,g6)
    c: Coincident(g7,g5)
    c: Weight(g8) = 1
    c: Equal(g8,g9)
    c: Equal(g8,g10)
    c: Coincident(g11,g4)
    c: InternalAlignment(g8,g11)
    c: InternalAlignment(g9,g11)
    c: InternalAlignment(g10,g11)
    c: InternalAlignment(g12,g11)
    c: InternalAlignment(g13,g11)
    c: Coincident(g17,g5)
    c: Weight(g14) = 1
    c: Equal(g14,g15)
    c: Equal(g14,g16)
    c: Coincident(g17,g3)
    c: InternalAlignment(g14,g17)
    c: InternalAlignment(g15,g17)
    c: InternalAlignment(g16,g17)
    c: InternalAlignment(g18,g17)
    c: InternalAlignment(g19,g17)
    c: Block(g7)
    c: Block(g17)
    c: Block(g11)
    c: Block(g6)
FEATURE [Part::Extrusion] Extrude003
  Base = -> Sketch002
  Dir = (0,0,1)
  DirMode = 2
  FaceMakerClass = Part::FaceMakerBullseye
  LengthFwd = 260
  LengthRev = 0
  Solid = true
  Symmetric = false
FEATURE [Part::Extrusion] Extrude
  Base = -> Sketch
  Dir = (0,0,1)
  DirMode = 2
  FaceMakerClass = Part::FaceMakerBullseye
  LengthFwd = 14
  LengthRev = 0
  Solid = true
  Symmetric = false
